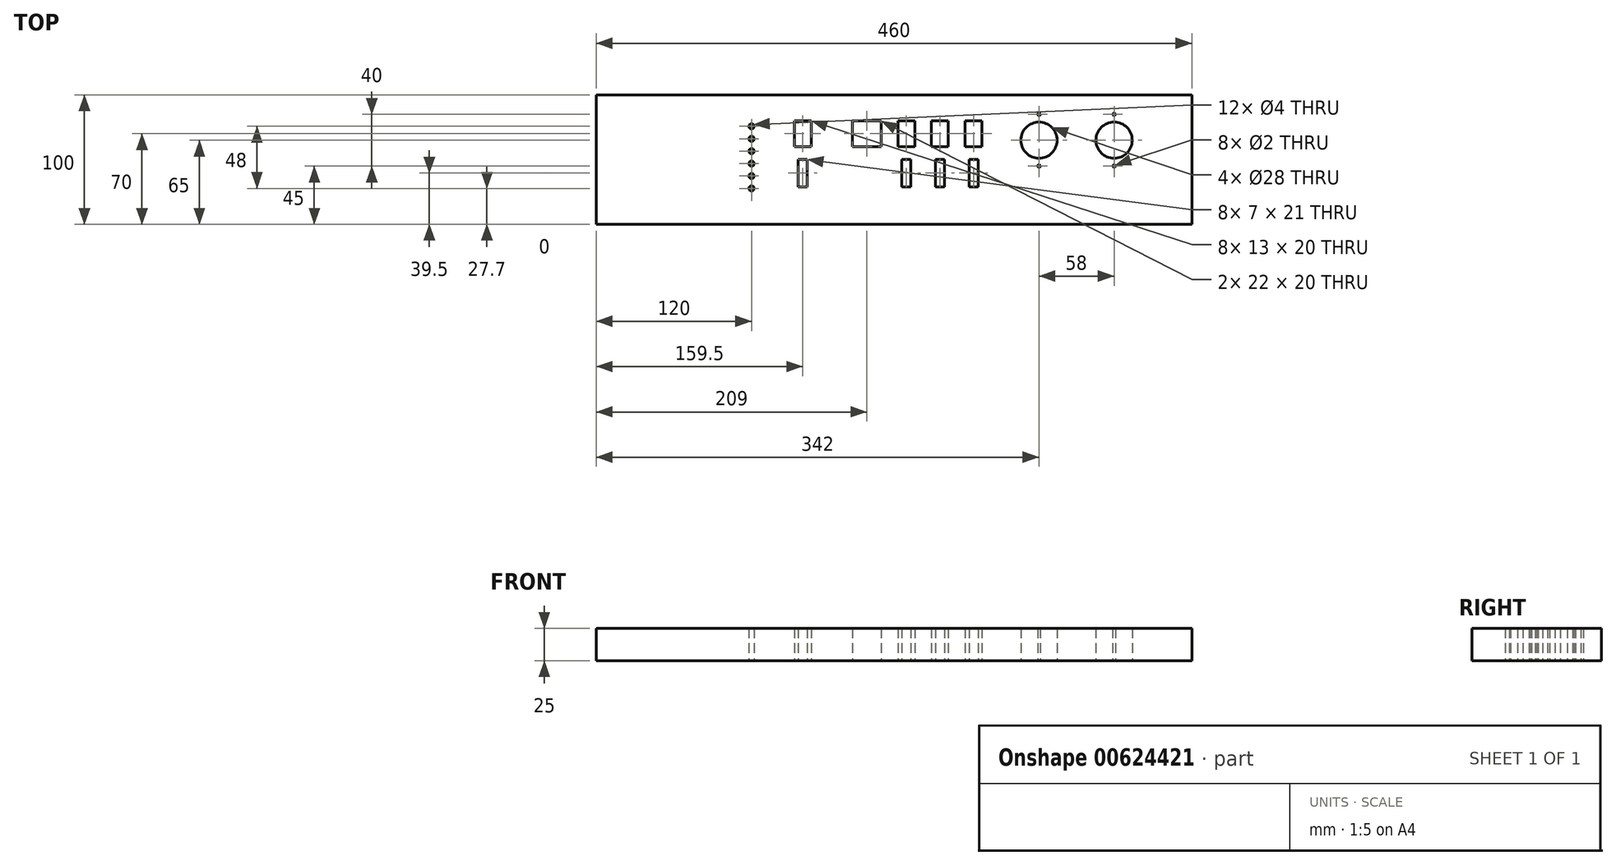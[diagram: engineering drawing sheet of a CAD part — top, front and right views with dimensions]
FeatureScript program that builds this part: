
annotation { "Feature Type Name" : "Feature", "Feature Type Description" : "" }
export const myFeature = defineFeature(function(context is Context, id is Id, definition is map)
    precondition{}
    {
        {
            var Q0;
            Q0=qCreatedBy(makeId("Top.planeOp"),FACE);
            var sketch = newSketch(context, id + "F0", { "sketchPlane" : qUnion([Q0])});
            skLineSegment(sketch, "E0.bottom", {"start": v(-460, 0) * mm, "end": v(0, 0) * mm});
            skLineSegment(sketch, "E0.top", {"start": v(-460, -100) * mm, "end": v(0, -100) * mm});
            skLineSegment(sketch, "E0.left", {"start": v(-460, 0) * mm, "end": v(-460, -100) * mm});
            skLineSegment(sketch, "E0.right", {"start": v(0, 0) * mm, "end": v(0, -100) * mm});
            skCircle(sketch, "E1", {"center": v(-340, -24.3) * mm, "radius": 2 * mm});
            skCircle(sketch, "E2", {"center": v(-340, -33.9) * mm, "radius": 2 * mm});
            skCircle(sketch, "E3", {"center": v(-340, -43.5) * mm, "radius": 2 * mm});
            skCircle(sketch, "E4", {"center": v(-340, -53.1) * mm, "radius": 2 * mm});
            skCircle(sketch, "E5", {"center": v(-340, -62.7) * mm, "radius": 2 * mm});
            skCircle(sketch, "E6", {"center": v(-340, -72.3) * mm, "radius": 2 * mm});
            skLineSegment(sketch, "E7.bottom", {"start": v(-307, -20) * mm, "end": v(-294, -20) * mm});
            skLineSegment(sketch, "E7.top", {"start": v(-307, -40) * mm, "end": v(-294, -40) * mm});
            skLineSegment(sketch, "E7.left", {"start": v(-307, -20) * mm, "end": v(-307, -40) * mm});
            skLineSegment(sketch, "E7.right", {"start": v(-294, -20) * mm, "end": v(-294, -40) * mm});
            skLineSegment(sketch, "E8.bottom", {"start": v(-262, -20) * mm, "end": v(-240, -20) * mm});
            skLineSegment(sketch, "E8.top", {"start": v(-262, -40) * mm, "end": v(-240, -40) * mm});
            skLineSegment(sketch, "E8.left", {"start": v(-262, -20) * mm, "end": v(-262, -40) * mm});
            skLineSegment(sketch, "E8.right", {"start": v(-240, -20) * mm, "end": v(-240, -40) * mm});
            skLineSegment(sketch, "E9.bottom", {"start": v(-227, -20) * mm, "end": v(-214, -20) * mm});
            skLineSegment(sketch, "E9.top", {"start": v(-227, -40) * mm, "end": v(-214, -40) * mm});
            skLineSegment(sketch, "E9.left", {"start": v(-227, -20) * mm, "end": v(-227, -40) * mm});
            skLineSegment(sketch, "E9.right", {"start": v(-214, -20) * mm, "end": v(-214, -40) * mm});
            skLineSegment(sketch, "E10.bottom", {"start": v(-175, -20) * mm, "end": v(-162, -20) * mm});
            skLineSegment(sketch, "E10.top", {"start": v(-175, -40) * mm, "end": v(-162, -40) * mm});
            skLineSegment(sketch, "E10.left", {"start": v(-175, -20) * mm, "end": v(-175, -40) * mm});
            skLineSegment(sketch, "E10.right", {"start": v(-162, -20) * mm, "end": v(-162, -40) * mm});
            skCircle(sketch, "E11", {"center": v(-118, -35) * mm, "radius": 14 * mm});
            skCircle(sketch, "E12", {"center": v(-60, -35) * mm, "radius": 14 * mm});
            skCircle(sketch, "E13", {"center": v(-118, -15) * mm, "radius": 1 * mm});
            skCircle(sketch, "E14", {"center": v(-60, -15) * mm, "radius": 1 * mm});
            skCircle(sketch, "E15", {"center": v(-60, -55) * mm, "radius": 1 * mm});
            skCircle(sketch, "E16", {"center": v(-118, -55) * mm, "radius": 1 * mm});
            skLineSegment(sketch, "E17.bottom", {"start": v(-201, -20) * mm, "end": v(-188, -20) * mm});
            skLineSegment(sketch, "E17.top", {"start": v(-201, -40) * mm, "end": v(-188, -40) * mm});
            skLineSegment(sketch, "E17.left", {"start": v(-201, -20) * mm, "end": v(-201, -40) * mm});
            skLineSegment(sketch, "E17.right", {"start": v(-188, -20) * mm, "end": v(-188, -40) * mm});
            skLineSegment(sketch, "E18.bottom", {"start": v(-304, -50) * mm, "end": v(-297, -50) * mm});
            skLineSegment(sketch, "E18.top", {"start": v(-304, -71) * mm, "end": v(-297, -71) * mm});
            skLineSegment(sketch, "E18.left", {"start": v(-304, -50) * mm, "end": v(-304, -71) * mm});
            skLineSegment(sketch, "E18.right", {"start": v(-297, -50) * mm, "end": v(-297, -71) * mm});
            skLineSegment(sketch, "E19.bottom", {"start": v(-224, -50) * mm, "end": v(-217, -50) * mm});
            skLineSegment(sketch, "E19.top", {"start": v(-224, -71) * mm, "end": v(-217, -71) * mm});
            skLineSegment(sketch, "E19.left", {"start": v(-224, -50) * mm, "end": v(-224, -71) * mm});
            skLineSegment(sketch, "E19.right", {"start": v(-217, -50) * mm, "end": v(-217, -71) * mm});
            skLineSegment(sketch, "E20.bottom", {"start": v(-198, -50) * mm, "end": v(-191, -50) * mm});
            skLineSegment(sketch, "E20.top", {"start": v(-198, -71) * mm, "end": v(-191, -71) * mm});
            skLineSegment(sketch, "E20.left", {"start": v(-198, -50) * mm, "end": v(-198, -71) * mm});
            skLineSegment(sketch, "E20.right", {"start": v(-191, -50) * mm, "end": v(-191, -71) * mm});
            skLineSegment(sketch, "E21.bottom", {"start": v(-172, -50) * mm, "end": v(-165, -50) * mm});
            skLineSegment(sketch, "E21.top", {"start": v(-172, -71) * mm, "end": v(-165, -71) * mm});
            skLineSegment(sketch, "E21.left", {"start": v(-172, -50) * mm, "end": v(-172, -71) * mm});
            skLineSegment(sketch, "E21.right", {"start": v(-165, -50) * mm, "end": v(-165, -71) * mm});
            skSolve(sketch);
        }
        {
            var Q0;
            Q0=makeQuery(id+"F0.imprint","IMPRINT",FACE,{"disambiguationData":[TD([[makeQuery(id+"F0.imprint","IMPRINT",EDGE,{"derivedFrom":sQuery(id+"F0.wireOp",EDGE,"E0.bottom")}),-1.0]])]});
            extrude(context, id + "F1", {"entities" : qUnion([Q0]), "depth" : 25 * mm, "offsetDistance" : 25 * mm});
        }
    });
